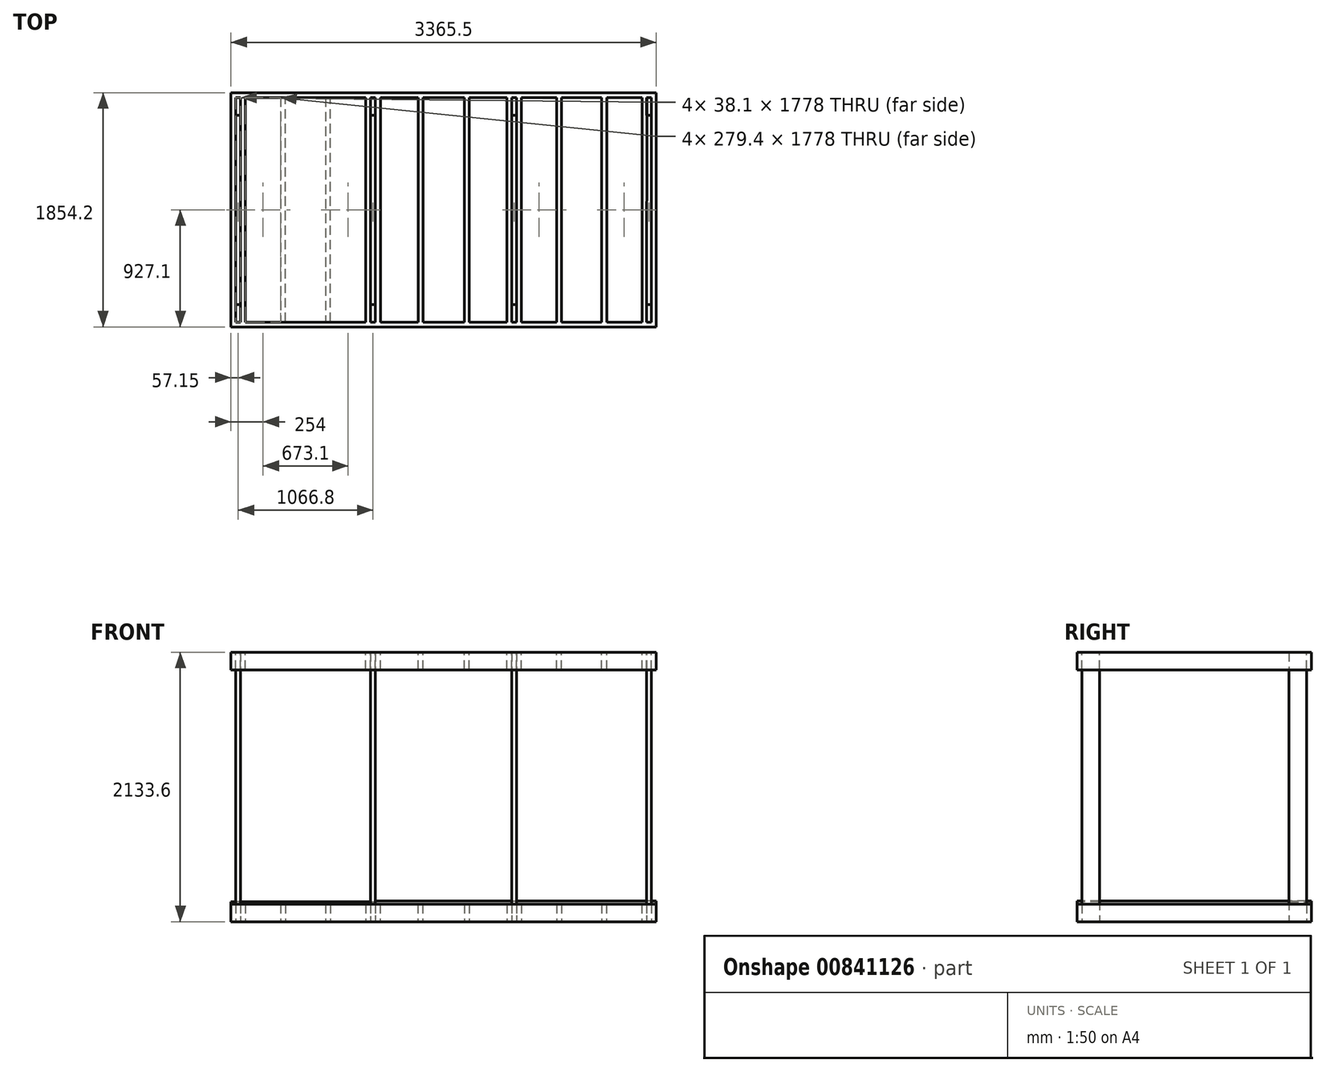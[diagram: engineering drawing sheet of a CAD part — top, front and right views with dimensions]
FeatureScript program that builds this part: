
annotation { "Feature Type Name" : "Feature", "Feature Type Description" : "" }
export const myFeature = defineFeature(function(context is Context, id is Id, definition is map)
    precondition{}
    {
        {
            var Q0;
            Q0=qCreatedBy(makeId("Top.planeOp"),FACE);
            var sketch = newSketch(context, id + "F0", { "sketchPlane" : qUnion([Q0])});
            skLineSegment(sketch, "E0.bottom", {"start": v(0, 0) * mm, "end": v(3365.5, 0) * mm});
            skLineSegment(sketch, "E0.top", {"start": v(0, -38.1) * mm, "end": v(1181.1, -38.1) * mm});
            skLineSegment(sketch, "E0.left", {"start": v(0, 0) * mm, "end": v(0, -38.1) * mm});
            skLineSegment(sketch, "E0.right", {"start": v(3365.5, 0) * mm, "end": v(3365.5, -38.1) * mm});
            skLineSegment(sketch, "E1.bottom", {"start": v(0, -38.1) * mm, "end": v(38.1, -38.1) * mm});
            skLineSegment(sketch, "E1.top", {"start": v(0, -1816.1) * mm, "end": v(38.1, -1816.1) * mm});
            skLineSegment(sketch, "E1.left", {"start": v(0, -38.1) * mm, "end": v(0, -1816.1) * mm});
            skLineSegment(sketch, "E1.right", {"start": v(38.1, -38.1) * mm, "end": v(38.1, -1816.1) * mm});
            skLineSegment(sketch, "E2.bottom", {"start": v(3251.2, -38.1) * mm, "end": v(3289.3, -38.1) * mm});
            skLineSegment(sketch, "E2.top", {"start": v(3251.2, -1816.1) * mm, "end": v(3289.3, -1816.1) * mm});
            skLineSegment(sketch, "E2.left", {"start": v(3251.2, -38.1) * mm, "end": v(3251.2, -1816.1) * mm});
            skLineSegment(sketch, "E2.right", {"start": v(3289.3, -38.1) * mm, "end": v(3289.3, -1816.1) * mm});
            skLineSegment(sketch, "E3.bottom", {"start": v(3365.5, -38.1) * mm, "end": v(3327.4, -38.1) * mm});
            skLineSegment(sketch, "E3.top", {"start": v(3365.5, -1816.1) * mm, "end": v(3327.4, -1816.1) * mm});
            skLineSegment(sketch, "E3.left", {"start": v(3365.5, -38.1) * mm, "end": v(3365.5, -1816.1) * mm});
            skLineSegment(sketch, "E3.right", {"start": v(3327.4, -38.1) * mm, "end": v(3327.4, -1816.1) * mm});
            skLineSegment(sketch, "E4.bottom", {"start": v(114.3, -38.1) * mm, "end": v(76.2, -38.1) * mm});
            skLineSegment(sketch, "E4.left", {"start": v(114.3, -38.1) * mm, "end": v(114.3, -1816.1) * mm});
            skLineSegment(sketch, "E4.right", {"start": v(76.2, -38.1) * mm, "end": v(76.2, -1816.1) * mm});
            skLineSegment(sketch, "E5.bottom", {"start": v(3365.5, -1854.2) * mm, "end": v(0, -1854.2) * mm});
            skLineSegment(sketch, "E5.top", {"start": v(3365.5, -1816.1) * mm, "end": v(0, -1816.1) * mm});
            skLineSegment(sketch, "E5.left", {"start": v(3365.5, -1816.1) * mm, "end": v(3365.5, -1854.2) * mm});
            skLineSegment(sketch, "E5.right", {"start": v(0, -1816.1) * mm, "end": v(0, -1854.2) * mm});
            skLineSegment(sketch, "E6.bottom", {"start": v(1066.8, -38.1) * mm, "end": v(1104.9, -38.1) * mm});
            skLineSegment(sketch, "E6.top", {"start": v(1066.8, -1816.1) * mm, "end": v(1104.9, -1816.1) * mm});
            skLineSegment(sketch, "E6.left", {"start": v(1066.8, -38.1) * mm, "end": v(1066.8, -1816.1) * mm});
            skLineSegment(sketch, "E6.right", {"start": v(1104.9, -38.1) * mm, "end": v(1104.9, -1816.1) * mm});
            skLineSegment(sketch, "E7.bottom", {"start": v(1143, -1816.1) * mm, "end": v(1181.1, -1816.1) * mm});
            skLineSegment(sketch, "E7.top", {"start": v(1143, -38.1) * mm, "end": v(1181.1, -38.1) * mm});
            skLineSegment(sketch, "E7.left", {"start": v(1143, -1816.1) * mm, "end": v(1143, -38.1) * mm});
            skLineSegment(sketch, "E7.right", {"start": v(1181.1, -1816.1) * mm, "end": v(1181.1, -38.1) * mm});
            skLineSegment(sketch, "E8.bottom", {"start": v(2184.4, -38.1) * mm, "end": v(2222.5, -38.1) * mm});
            skLineSegment(sketch, "E8.top", {"start": v(2184.4, -1816.1) * mm, "end": v(2222.5, -1816.1) * mm});
            skLineSegment(sketch, "E8.left", {"start": v(2184.4, -38.1) * mm, "end": v(2184.4, -1816.1) * mm});
            skLineSegment(sketch, "E8.right", {"start": v(2222.5, -38.1) * mm, "end": v(2222.5, -1816.1) * mm});
            skLineSegment(sketch, "E9.bottom", {"start": v(2260.6, -38.1) * mm, "end": v(2298.7, -38.1) * mm});
            skLineSegment(sketch, "E9.top", {"start": v(2260.6, -1816.1) * mm, "end": v(2298.7, -1816.1) * mm});
            skLineSegment(sketch, "E9.left", {"start": v(2260.6, -38.1) * mm, "end": v(2260.6, -1816.1) * mm});
            skLineSegment(sketch, "E9.right", {"start": v(2298.7, -38.1) * mm, "end": v(2298.7, -1816.1) * mm});
            skLineSegment(sketch, "E10", {"start": v(1123.95, -38.1) * mm, "end": v(1123.95, -1816.1) * mm, "construction": true});
            skLineSegment(sketch, "E11", {"start": v(2241.55, -38.1) * mm, "end": v(2241.55, -1816.1) * mm, "construction": true});
            skLineSegment(sketch, "E12", {"start": v(1181.1, -38.1) * mm, "end": v(3365.5, -38.1) * mm});
            skLineSegment(sketch, "E13", {"start": v(57.15, -38.1) * mm, "end": v(57.15, -1816.1) * mm, "construction": true});
            skLineSegment(sketch, "E14", {"start": v(3308.35, -38.1) * mm, "end": v(3308.35, -1816.1) * mm, "construction": true});
            skLineSegment(sketch, "E15", {"start": v(412.75, -38.1) * mm, "end": v(412.75, -1816.1) * mm, "construction": true});
            skLineSegment(sketch, "E16", {"start": v(768.35, -38.1) * mm, "end": v(768.35, -1816.1) * mm, "construction": true});
            skLineSegment(sketch, "E17", {"start": v(1498.6, -38.1) * mm, "end": v(1498.6, -1816.1) * mm, "construction": true});
            skLineSegment(sketch, "E18", {"start": v(1866.9, -38.1) * mm, "end": v(1866.9, -1816.1) * mm, "construction": true});
            skLineSegment(sketch, "E19", {"start": v(2597.15, -38.1) * mm, "end": v(2597.15, -1816.1) * mm, "construction": true});
            skLineSegment(sketch, "E20", {"start": v(2952.75, -38.1) * mm, "end": v(2952.75, -1816.1) * mm, "construction": true});
            skLineSegment(sketch, "E21", {"start": v(412.75, -927.1) * mm, "end": v(57.15, -927.1) * mm, "construction": true});
            skLineSegment(sketch, "E22", {"start": v(412.75, -927.1) * mm, "end": v(768.35, -927.1) * mm, "construction": true});
            skLineSegment(sketch, "E23", {"start": v(768.35, -927.1) * mm, "end": v(1123.95, -927.1) * mm, "construction": true});
            skLineSegment(sketch, "E24", {"start": v(1123.95, -927.1) * mm, "end": v(1498.6, -927.1) * mm, "construction": true});
            skLineSegment(sketch, "E25", {"start": v(1498.6, -927.1) * mm, "end": v(1866.9, -927.1) * mm, "construction": true});
            skLineSegment(sketch, "E26", {"start": v(1866.9, -927.1) * mm, "end": v(2241.55, -927.1) * mm, "construction": true});
            skLineSegment(sketch, "E27", {"start": v(2241.55, -927.1) * mm, "end": v(2597.15, -927.1) * mm, "construction": true});
            skLineSegment(sketch, "E28", {"start": v(2597.15, -927.1) * mm, "end": v(2952.75, -927.1) * mm, "construction": true});
            skLineSegment(sketch, "E29", {"start": v(2952.75, -927.1) * mm, "end": v(3308.35, -927.1) * mm, "construction": true});
            skLineSegment(sketch, "E30", {"start": v(393.7, -38.1) * mm, "end": v(393.7, -1816.1) * mm});
            skLineSegment(sketch, "E31", {"start": v(431.8, -1816.1) * mm, "end": v(431.8, -38.1) * mm});
            skLineSegment(sketch, "E32", {"start": v(749.3, -38.1) * mm, "end": v(749.3, -1816.1) * mm});
            skLineSegment(sketch, "E33", {"start": v(787.4, -1816.1) * mm, "end": v(787.4, -38.1) * mm});
            skLineSegment(sketch, "E34", {"start": v(1479.55, -38.1) * mm, "end": v(1479.55, -1816.1) * mm});
            skLineSegment(sketch, "E35", {"start": v(1517.65, -1816.1) * mm, "end": v(1517.65, -38.1) * mm});
            skLineSegment(sketch, "E36", {"start": v(1847.85, -38.1) * mm, "end": v(1847.85, -1816.1) * mm});
            skLineSegment(sketch, "E37", {"start": v(1885.95, -1816.1) * mm, "end": v(1885.95, -38.1) * mm});
            skLineSegment(sketch, "E38", {"start": v(2578.1, -38.1) * mm, "end": v(2578.1, -1816.1) * mm});
            skLineSegment(sketch, "E39", {"start": v(2616.2, -1816.1) * mm, "end": v(2616.2, -38.1) * mm});
            skLineSegment(sketch, "E40", {"start": v(2933.7, -38.1) * mm, "end": v(2933.7, -1816.1) * mm});
            skLineSegment(sketch, "E41", {"start": v(2971.8, -1816.1) * mm, "end": v(2971.8, -38.1) * mm});
            skLineSegment(sketch, "E42", {"start": v(393.7, -447.33) * mm, "end": v(412.75, -447.33) * mm, "construction": true});
            skLineSegment(sketch, "E43", {"start": v(412.75, -447.33) * mm, "end": v(431.8, -447.33) * mm, "construction": true});
            skLineSegment(sketch, "E44", {"start": v(768.35, -464.24) * mm, "end": v(787.4, -464.24) * mm, "construction": true});
            skLineSegment(sketch, "E45", {"start": v(1479.55, -447.33) * mm, "end": v(1498.6, -447.33) * mm, "construction": true});
            skLineSegment(sketch, "E46", {"start": v(1498.6, -447.33) * mm, "end": v(1517.65, -447.33) * mm, "construction": true});
            skLineSegment(sketch, "E47", {"start": v(1866.9, -447.33) * mm, "end": v(1885.95, -447.33) * mm, "construction": true});
            skLineSegment(sketch, "E48", {"start": v(1847.85, -447.33) * mm, "end": v(1866.9, -447.33) * mm, "construction": true});
            skLineSegment(sketch, "E49", {"start": v(2578.1, -447.33) * mm, "end": v(2597.15, -447.33) * mm, "construction": true});
            skLineSegment(sketch, "E50", {"start": v(2597.15, -447.33) * mm, "end": v(2616.2, -447.33) * mm, "construction": true});
            skLineSegment(sketch, "E51", {"start": v(2933.7, -447.33) * mm, "end": v(2952.75, -447.33) * mm, "construction": true});
            skLineSegment(sketch, "E52", {"start": v(2952.75, -447.33) * mm, "end": v(2971.8, -447.33) * mm, "construction": true});
            skLineSegment(sketch, "E53", {"start": v(768.35, -464.24) * mm, "end": v(749.3, -464.24) * mm, "construction": true});
            skSolve(sketch);
        }
        {
            var Q0;
            Q0=makeQuery(id+"F0.imprint","IMPRINT",FACE,{"disambiguationData":[TD([[makeQuery(id+"F0.imprint","IMPRINT",EDGE,{"derivedFrom":sQuery(id+"F0.wireOp",EDGE,"E0.bottom")}),-1.0]])]});
            var Q1;
            Q1=makeQuery(id+"F0.imprint","IMPRINT",FACE,{"disambiguationData":[TD([[makeQuery(id+"F0.imprint","IMPRINT",EDGE,{"derivedFrom":sQuery(id+"F0.wireOp",EDGE,"E3.bottom")}),1.0]])]});
            var Q2;
            Q2=makeQuery(id+"F0.imprint","IMPRINT",FACE,{"disambiguationData":[TD([[makeQuery(id+"F0.imprint","IMPRINT",EDGE,{"derivedFrom":sQuery(id+"F0.wireOp",EDGE,"E2.bottom")}),-1.0]])]});
            var Q3;
            {var subQ18=sQuery(id+"F0.wireOp",EDGE,"E1.top");Q3=makeQuery(id+"F0.imprint","IMPRINT",FACE,{"disambiguationData":[TD([[makeQuery(id+"F0.imprint","IMPRINT",EDGE,{"derivedFrom":subQ18}),-1.0]])]});}
            var Q4;
            Q4=makeQuery(id+"F0.imprint","IMPRINT",FACE,{"disambiguationData":[TD([[makeQuery(id+"F0.imprint","IMPRINT",EDGE,{"derivedFrom":sQuery(id+"F0.wireOp",EDGE,"E1.top")}),1.0]])]});
            var Q5;
            {var subQ2=sQuery(id+"F0.wireOp",EDGE,"E4.left");Q5=makeQuery(id+"F0.imprint","IMPRINT",FACE,{"disambiguationData":[TD([[makeQuery(id+"F0.imprint","IMPRINT",EDGE,{"derivedFrom":subQ2}),-1.0]])]});}
            var Q6;
            {var subQ0=sQuery(id+"F0.wireOp",EDGE,"E6.left");Q6=makeQuery(id+"F0.imprint","IMPRINT",FACE,{"disambiguationData":[TD([[makeQuery(id+"F0.imprint","IMPRINT",EDGE,{"derivedFrom":subQ0}),1.0]])]});}
            var Q7;
            {var subQ0=sQuery(id+"F0.wireOp",EDGE,"E7.left");Q7=makeQuery(id+"F0.imprint","IMPRINT",FACE,{"disambiguationData":[TD([[makeQuery(id+"F0.imprint","IMPRINT",EDGE,{"derivedFrom":subQ0}),-1.0]])]});}
            var Q8;
            Q8=makeQuery(id+"F0.imprint","IMPRINT",FACE,{"disambiguationData":[TD([[makeQuery(id+"F0.imprint","IMPRINT",EDGE,{"derivedFrom":sQuery(id+"F0.wireOp",EDGE,"E8.bottom")}),-1.0]])]});
            var Q9;
            Q9=makeQuery(id+"F0.imprint","IMPRINT",FACE,{"disambiguationData":[TD([[makeQuery(id+"F0.imprint","IMPRINT",EDGE,{"derivedFrom":sQuery(id+"F0.wireOp",EDGE,"E9.bottom")}),-1.0]])]});
            var Q10;
            Q10=makeQuery(id+"F0.imprint","IMPRINT",FACE,{"disambiguationData":[TD([[makeQuery(id+"F0.imprint","IMPRINT",EDGE,{"derivedFrom":sQuery(id+"F0.wireOp",EDGE,"E2.bottom")}),-1.0]])]});
            var Q11;
            Q11=makeQuery(id+"F0.imprint","IMPRINT",FACE,{"disambiguationData":[TD([[makeQuery(id+"F0.imprint","IMPRINT",EDGE,{"derivedFrom":sQuery(id+"F0.wireOp",EDGE,"E3.bottom")}),1.0]])]});
            var Q12;
            {var subQ2=sQuery(id+"F0.wireOp",EDGE,"E30");Q12=makeQuery(id+"F0.imprint","IMPRINT",FACE,{"disambiguationData":[TD([[makeQuery(id+"F0.imprint","IMPRINT",EDGE,{"derivedFrom":subQ2}),1.0]])]});}
            var Q13;
            {var subQ0=sQuery(id+"F0.wireOp",EDGE,"E32");Q13=makeQuery(id+"F0.imprint","IMPRINT",FACE,{"disambiguationData":[TD([[makeQuery(id+"F0.imprint","IMPRINT",EDGE,{"derivedFrom":subQ0}),1.0]])]});}
            var Q14;
            {var subQ0=sQuery(id+"F0.wireOp",EDGE,"E34");Q14=makeQuery(id+"F0.imprint","IMPRINT",FACE,{"disambiguationData":[TD([[makeQuery(id+"F0.imprint","IMPRINT",EDGE,{"derivedFrom":subQ0}),1.0]])]});}
            var Q15;
            {var subQ0=sQuery(id+"F0.wireOp",EDGE,"E36");Q15=makeQuery(id+"F0.imprint","IMPRINT",FACE,{"disambiguationData":[TD([[makeQuery(id+"F0.imprint","IMPRINT",EDGE,{"derivedFrom":subQ0}),1.0]])]});}
            var Q16;
            {var subQ0=sQuery(id+"F0.wireOp",EDGE,"E38");Q16=makeQuery(id+"F0.imprint","IMPRINT",FACE,{"disambiguationData":[TD([[makeQuery(id+"F0.imprint","IMPRINT",EDGE,{"derivedFrom":subQ0}),1.0]])]});}
            var Q17;
            {var subQ0=sQuery(id+"F0.wireOp",EDGE,"E40");Q17=makeQuery(id+"F0.imprint","IMPRINT",FACE,{"disambiguationData":[TD([[makeQuery(id+"F0.imprint","IMPRINT",EDGE,{"derivedFrom":subQ0}),1.0]])]});}
            extrude(context, id + "F1", {"entities" : qUnion([Q0, Q1, Q2, Q3, Q4, Q5, Q6, Q7, Q8, Q9, Q10, Q11, Q12, Q13, Q14, Q15, Q16, Q17]), "depth" : 139.7 * mm, "offsetDistance" : 25.4 * mm});
        }
        {
            var Q0;
            Q0=makeQuery(id+"F1.opExtrude","CAP_FACE",FACE,{"disambiguationData":[OSD([sQuery(id+"F0.wireOp",EDGE,"E0.bottom"),sQuery(id+"F0.wireOp",EDGE,"E0.top"),sQuery(id+"F0.wireOp",EDGE,"E0.left"),sQuery(id+"F0.wireOp",EDGE,"E0.right"),sQuery(id+"F0.wireOp",EDGE,"E1.left"),sQuery(id+"F0.wireOp",EDGE,"E1.right"),sQuery(id+"F0.wireOp",EDGE,"E2.left"),sQuery(id+"F0.wireOp",EDGE,"E2.right"),sQuery(id+"F0.wireOp",EDGE,"E3.left"),sQuery(id+"F0.wireOp",EDGE,"E3.right"),sQuery(id+"F0.wireOp",EDGE,"E4.left"),sQuery(id+"F0.wireOp",EDGE,"E4.right"),sQuery(id+"F0.wireOp",EDGE,"E5.bottom"),sQuery(id+"F0.wireOp",EDGE,"E5.top"),sQuery(id+"F0.wireOp",EDGE,"E5.left"),sQuery(id+"F0.wireOp",EDGE,"E5.right"),sQuery(id+"F0.wireOp",EDGE,"E6.left"),sQuery(id+"F0.wireOp",EDGE,"E6.right"),sQuery(id+"F0.wireOp",EDGE,"E7.left"),sQuery(id+"F0.wireOp",EDGE,"E7.right"),sQuery(id+"F0.wireOp",EDGE,"E8.left"),sQuery(id+"F0.wireOp",EDGE,"E8.right"),sQuery(id+"F0.wireOp",EDGE,"E9.left"),sQuery(id+"F0.wireOp",EDGE,"E9.right"),sQuery(id+"F0.wireOp",EDGE,"E12"),sQuery(id+"F0.wireOp",EDGE,"E30"),sQuery(id+"F0.wireOp",EDGE,"E31"),sQuery(id+"F0.wireOp",EDGE,"E32"),sQuery(id+"F0.wireOp",EDGE,"E33"),sQuery(id+"F0.wireOp",EDGE,"E34"),sQuery(id+"F0.wireOp",EDGE,"E35"),sQuery(id+"F0.wireOp",EDGE,"E36"),sQuery(id+"F0.wireOp",EDGE,"E37"),sQuery(id+"F0.wireOp",EDGE,"E38"),sQuery(id+"F0.wireOp",EDGE,"E39"),sQuery(id+"F0.wireOp",EDGE,"E40"),sQuery(id+"F0.wireOp",EDGE,"E41")])],"isStart":true});
            var sketch = newSketch(context, id + "F2", { "sketchPlane" : qUnion([Q0])});
            skLineSegment(sketch, "E54.bottom", {"start": v(38.1, 1816.1) * mm, "end": v(76.2, 1816.1) * mm});
            skLineSegment(sketch, "E54.top", {"start": v(38.1, 1676.4) * mm, "end": v(76.2, 1676.4) * mm});
            skLineSegment(sketch, "E54.left", {"start": v(38.1, 1816.1) * mm, "end": v(38.1, 1676.4) * mm});
            skLineSegment(sketch, "E54.right", {"start": v(76.2, 1816.1) * mm, "end": v(76.2, 1676.4) * mm});
            skLineSegment(sketch, "E55.bottom", {"start": v(1104.9, 1816.1) * mm, "end": v(1143, 1816.1) * mm});
            skLineSegment(sketch, "E55.top", {"start": v(1104.9, 1676.4) * mm, "end": v(1143, 1676.4) * mm});
            skLineSegment(sketch, "E55.left", {"start": v(1104.9, 1816.1) * mm, "end": v(1104.9, 1676.4) * mm});
            skLineSegment(sketch, "E55.right", {"start": v(1143, 1816.1) * mm, "end": v(1143, 1676.4) * mm});
            skLineSegment(sketch, "E56.bottom", {"start": v(2222.5, 1816.1) * mm, "end": v(2260.6, 1816.1) * mm});
            skLineSegment(sketch, "E56.top", {"start": v(2222.5, 1676.4) * mm, "end": v(2260.6, 1676.4) * mm});
            skLineSegment(sketch, "E56.left", {"start": v(2222.5, 1816.1) * mm, "end": v(2222.5, 1676.4) * mm});
            skLineSegment(sketch, "E56.right", {"start": v(2260.6, 1816.1) * mm, "end": v(2260.6, 1676.4) * mm});
            skLineSegment(sketch, "E57.bottom", {"start": v(3289.3, 1816.1) * mm, "end": v(3327.4, 1816.1) * mm});
            skLineSegment(sketch, "E57.top", {"start": v(3289.3, 1676.4) * mm, "end": v(3327.4, 1676.4) * mm});
            skLineSegment(sketch, "E57.left", {"start": v(3289.3, 1816.1) * mm, "end": v(3289.3, 1676.4) * mm});
            skLineSegment(sketch, "E57.right", {"start": v(3327.4, 1816.1) * mm, "end": v(3327.4, 1676.4) * mm});
            skLineSegment(sketch, "E58.bottom", {"start": v(3289.3, 38.1) * mm, "end": v(3327.4, 38.1) * mm});
            skLineSegment(sketch, "E58.top", {"start": v(3289.3, 177.8) * mm, "end": v(3327.4, 177.8) * mm});
            skLineSegment(sketch, "E58.left", {"start": v(3289.3, 38.1) * mm, "end": v(3289.3, 177.8) * mm});
            skLineSegment(sketch, "E58.right", {"start": v(3327.4, 38.1) * mm, "end": v(3327.4, 177.8) * mm});
            skLineSegment(sketch, "E59.bottom", {"start": v(2222.5, 38.1) * mm, "end": v(2260.6, 38.1) * mm});
            skLineSegment(sketch, "E59.top", {"start": v(2222.5, 177.8) * mm, "end": v(2260.6, 177.8) * mm});
            skLineSegment(sketch, "E59.left", {"start": v(2222.5, 38.1) * mm, "end": v(2222.5, 177.8) * mm});
            skLineSegment(sketch, "E59.right", {"start": v(2260.6, 38.1) * mm, "end": v(2260.6, 177.8) * mm});
            skLineSegment(sketch, "E60.bottom", {"start": v(1104.9, 38.1) * mm, "end": v(1143, 38.1) * mm});
            skLineSegment(sketch, "E60.top", {"start": v(1104.9, 177.8) * mm, "end": v(1143, 177.8) * mm});
            skLineSegment(sketch, "E60.left", {"start": v(1104.9, 38.1) * mm, "end": v(1104.9, 177.8) * mm});
            skLineSegment(sketch, "E60.right", {"start": v(1143, 38.1) * mm, "end": v(1143, 177.8) * mm});
            skLineSegment(sketch, "E61.bottom", {"start": v(38.1, 38.1) * mm, "end": v(76.2, 38.1) * mm});
            skLineSegment(sketch, "E61.top", {"start": v(38.1, 177.8) * mm, "end": v(76.2, 177.8) * mm});
            skLineSegment(sketch, "E61.left", {"start": v(38.1, 38.1) * mm, "end": v(38.1, 177.8) * mm});
            skLineSegment(sketch, "E61.right", {"start": v(76.2, 38.1) * mm, "end": v(76.2, 177.8) * mm});
            skSolve(sketch);
        }
        {
            var Q0;
            Q0=makeQuery(id+"F2.imprint","IMPRINT",FACE,{"disambiguationData":[TD([[makeQuery(id+"F2.imprint","IMPRINT",EDGE,{"derivedFrom":sQuery(id+"F2.wireOp",EDGE,"E61.bottom")}),1.0]])]});
            var Q1;
            Q1=makeQuery(id+"F2.imprint","IMPRINT",FACE,{"disambiguationData":[TD([[makeQuery(id+"F2.imprint","IMPRINT",EDGE,{"derivedFrom":sQuery(id+"F2.wireOp",EDGE,"E60.bottom")}),1.0]])]});
            var Q2;
            Q2=makeQuery(id+"F2.imprint","IMPRINT",FACE,{"disambiguationData":[TD([[makeQuery(id+"F2.imprint","IMPRINT",EDGE,{"derivedFrom":sQuery(id+"F2.wireOp",EDGE,"E59.bottom")}),1.0]])]});
            var Q3;
            Q3=makeQuery(id+"F2.imprint","IMPRINT",FACE,{"disambiguationData":[TD([[makeQuery(id+"F2.imprint","IMPRINT",EDGE,{"derivedFrom":sQuery(id+"F2.wireOp",EDGE,"E58.bottom")}),1.0]])]});
            var Q4;
            Q4=makeQuery(id+"F2.imprint","IMPRINT",FACE,{"disambiguationData":[TD([[makeQuery(id+"F2.imprint","IMPRINT",EDGE,{"derivedFrom":sQuery(id+"F2.wireOp",EDGE,"E54.bottom")}),1.0]])]});
            var Q5;
            Q5=makeQuery(id+"F2.imprint","IMPRINT",FACE,{"disambiguationData":[TD([[makeQuery(id+"F2.imprint","IMPRINT",EDGE,{"derivedFrom":sQuery(id+"F2.wireOp",EDGE,"E55.bottom")}),1.0]])]});
            var Q6;
            Q6=makeQuery(id+"F2.imprint","IMPRINT",FACE,{"disambiguationData":[TD([[makeQuery(id+"F2.imprint","IMPRINT",EDGE,{"derivedFrom":sQuery(id+"F2.wireOp",EDGE,"E56.bottom")}),1.0]])]});
            var Q7;
            Q7=makeQuery(id+"F2.imprint","IMPRINT",FACE,{"disambiguationData":[TD([[makeQuery(id+"F2.imprint","IMPRINT",EDGE,{"derivedFrom":sQuery(id+"F2.wireOp",EDGE,"E57.bottom")}),1.0]])]});
            extrude(context, id + "F3", {"entities" : qUnion([Q0, Q1, Q2, Q3, Q4, Q5, Q6, Q7]), "oppositeDirection" : true, "depth" : 2133.6 * mm, "offsetDistance" : 25.4 * mm});
        }
        {
            var Q0;
            Q0=makeQuery(id+"F3.opExtrude","CAP_FACE",FACE,{"disambiguationData":[OSD([sQuery(id+"F2.wireOp",EDGE,"E57.bottom"),sQuery(id+"F2.wireOp",EDGE,"E57.top"),sQuery(id+"F2.wireOp",EDGE,"E57.left"),sQuery(id+"F2.wireOp",EDGE,"E57.right")])],"isStart":false});
            var sketch = newSketch(context, id + "F4", { "sketchPlane" : qUnion([Q0])});
            skLineSegment(sketch, "E62", {"start": v(3327.4, -1816.1) * mm, "end": v(38.1, -1816.1) * mm});
            skLineSegment(sketch, "E63", {"start": v(38.1, -1816.1) * mm, "end": v(38.1, -38.1) * mm});
            skLineSegment(sketch, "E64", {"start": v(38.1, -38.1) * mm, "end": v(3327.4, -38.1) * mm});
            skLineSegment(sketch, "E65", {"start": v(3327.4, -38.1) * mm, "end": v(3327.4, -1816.1) * mm});
            skLineSegment(sketch, "E66", {"start": v(3365.5, -1854.2) * mm, "end": v(3365.5, 0) * mm});
            skLineSegment(sketch, "E67", {"start": v(3365.5, 0) * mm, "end": v(0, 0) * mm});
            skLineSegment(sketch, "E68", {"start": v(0, 0) * mm, "end": v(0, -1854.2) * mm});
            skLineSegment(sketch, "E69", {"start": v(0, -1854.2) * mm, "end": v(3365.5, -1854.2) * mm});
            skLineSegment(sketch, "E70", {"start": v(3290.38, -38.1) * mm, "end": v(3289.3, -1816.1) * mm});
            skLineSegment(sketch, "E71", {"start": v(3252.14, -1816.1) * mm, "end": v(3252.14, -38.1) * mm});
            skLineSegment(sketch, "E72", {"start": v(2972.63, -38.1) * mm, "end": v(2972.63, -1816.1) * mm});
            skLineSegment(sketch, "E73", {"start": v(2933.24, -1816.1) * mm, "end": v(2933.24, -38.1) * mm});
            skLineSegment(sketch, "E74", {"start": v(2616.6, -38.1) * mm, "end": v(2616.6, -1816.1) * mm});
            skLineSegment(sketch, "E75", {"start": v(2577.63, -1816.1) * mm, "end": v(2577.63, -38.1) * mm});
            skLineSegment(sketch, "E76", {"start": v(2299.35, -38.1) * mm, "end": v(2299.35, -1816.1) * mm});
            skLineSegment(sketch, "E77", {"start": v(2260.87, -1816.1) * mm, "end": v(2260.87, -38.1) * mm});
            skLineSegment(sketch, "E78", {"start": v(2222.09, -38.1) * mm, "end": v(2222.09, -1816.1) * mm});
            skLineSegment(sketch, "E79", {"start": v(2184.41, -1816.1) * mm, "end": v(2184.41, -38.1) * mm});
            skLineSegment(sketch, "E80", {"start": v(1886.34, -38.1) * mm, "end": v(1886.34, -1816.1) * mm});
            skLineSegment(sketch, "E81", {"start": v(1848.29, -1816.1) * mm, "end": v(1848.29, -38.1) * mm});
            skLineSegment(sketch, "E82", {"start": v(1518.71, -38.1) * mm, "end": v(1518.71, -1816.1) * mm});
            skLineSegment(sketch, "E83", {"start": v(1480.52, -1816.1) * mm, "end": v(1480.52, -38.1) * mm});
            skLineSegment(sketch, "E84", {"start": v(1183.17, -38.1) * mm, "end": v(1183.17, -1816.1) * mm});
            skLineSegment(sketch, "E85", {"start": v(1143.26, -1816.1) * mm, "end": v(1143.26, -38.1) * mm});
            skLineSegment(sketch, "E86", {"start": v(1105.01, -1816.1) * mm, "end": v(1105.01, -38.1) * mm});
            skLineSegment(sketch, "E87", {"start": v(1065.91, -38.1) * mm, "end": v(1065.91, -1816.1) * mm});
            skLineSegment(sketch, "E88", {"start": v(76.3, -1816.1) * mm, "end": v(76.3, -38.1) * mm});
            skLineSegment(sketch, "E89", {"start": v(114.7, -38.1) * mm, "end": v(114.7, -1816.1) * mm});
            skSolve(sketch);
        }
        {
            var Q0;
            Q0 = qSketchRegion(id + "F4", true);
            var Q1;
            {var subQ5=sQuery(id+"F4.wireOp",EDGE,"E71");Q1=makeQuery(id+"F4.imprint","IMPRINT",FACE,{"disambiguationData":[TD([[makeQuery(id+"F4.imprint","IMPRINT",EDGE,{"derivedFrom":subQ5}),-1.0]])]});}
            var Q2;
            {var subQ0=sQuery(id+"F4.wireOp",EDGE,"E72");Q2=makeQuery(id+"F4.imprint","IMPRINT",FACE,{"disambiguationData":[TD([[makeQuery(id+"F4.imprint","IMPRINT",EDGE,{"derivedFrom":subQ0}),-1.0]])]});}
            var Q3;
            {var subQ0=sQuery(id+"F4.wireOp",EDGE,"E74");Q3=makeQuery(id+"F4.imprint","IMPRINT",FACE,{"disambiguationData":[TD([[makeQuery(id+"F4.imprint","IMPRINT",EDGE,{"derivedFrom":subQ0}),-1.0]])]});}
            var Q4;
            {var subQ0=sQuery(id+"F4.wireOp",EDGE,"E76");Q4=makeQuery(id+"F4.imprint","IMPRINT",FACE,{"disambiguationData":[TD([[makeQuery(id+"F4.imprint","IMPRINT",EDGE,{"derivedFrom":subQ0}),-1.0]])]});}
            var Q5;
            {var subQ0=sQuery(id+"F4.wireOp",EDGE,"E78");Q5=makeQuery(id+"F4.imprint","IMPRINT",FACE,{"disambiguationData":[TD([[makeQuery(id+"F4.imprint","IMPRINT",EDGE,{"derivedFrom":subQ0}),-1.0]])]});}
            var Q6;
            {var subQ0=sQuery(id+"F4.wireOp",EDGE,"E80");Q6=makeQuery(id+"F4.imprint","IMPRINT",FACE,{"disambiguationData":[TD([[makeQuery(id+"F4.imprint","IMPRINT",EDGE,{"derivedFrom":subQ0}),-1.0]])]});}
            var Q7;
            {var subQ0=sQuery(id+"F4.wireOp",EDGE,"E82");Q7=makeQuery(id+"F4.imprint","IMPRINT",FACE,{"disambiguationData":[TD([[makeQuery(id+"F4.imprint","IMPRINT",EDGE,{"derivedFrom":subQ0}),-1.0]])]});}
            var Q8;
            {var subQ0=sQuery(id+"F4.wireOp",EDGE,"E84");Q8=makeQuery(id+"F4.imprint","IMPRINT",FACE,{"disambiguationData":[TD([[makeQuery(id+"F4.imprint","IMPRINT",EDGE,{"derivedFrom":subQ0}),-1.0]])]});}
            var Q9;
            {var subQ0=sQuery(id+"F4.wireOp",EDGE,"E86");Q9=makeQuery(id+"F4.imprint","IMPRINT",FACE,{"disambiguationData":[TD([[makeQuery(id+"F4.imprint","IMPRINT",EDGE,{"derivedFrom":subQ0}),1.0]])]});}
            var Q10;
            {var subQ0=sQuery(id+"F4.wireOp",EDGE,"E88");Q10=makeQuery(id+"F4.imprint","IMPRINT",FACE,{"disambiguationData":[TD([[makeQuery(id+"F4.imprint","IMPRINT",EDGE,{"derivedFrom":subQ0}),-1.0]])]});}
            extrude(context, id + "F5", {"entities" : qUnion([Q0, Q1, Q2, Q3, Q4, Q5, Q6, Q7, Q8, Q9, Q10]), "oppositeDirection" : true, "depth" : 139.7 * mm, "offsetDistance" : 25.4 * mm});
        }
        {
            var Q0;
            Q0=makeQuery(id+"F1.opExtrude","CAP_FACE",FACE,{"disambiguationData":[OSD([sQuery(id+"F0.wireOp",EDGE,"E0.bottom"),sQuery(id+"F0.wireOp",EDGE,"E0.top"),sQuery(id+"F0.wireOp",EDGE,"E0.left"),sQuery(id+"F0.wireOp",EDGE,"E0.right"),sQuery(id+"F0.wireOp",EDGE,"E1.left"),sQuery(id+"F0.wireOp",EDGE,"E1.right"),sQuery(id+"F0.wireOp",EDGE,"E2.left"),sQuery(id+"F0.wireOp",EDGE,"E2.right"),sQuery(id+"F0.wireOp",EDGE,"E3.left"),sQuery(id+"F0.wireOp",EDGE,"E3.right"),sQuery(id+"F0.wireOp",EDGE,"E4.left"),sQuery(id+"F0.wireOp",EDGE,"E4.right"),sQuery(id+"F0.wireOp",EDGE,"E5.bottom"),sQuery(id+"F0.wireOp",EDGE,"E5.top"),sQuery(id+"F0.wireOp",EDGE,"E5.left"),sQuery(id+"F0.wireOp",EDGE,"E5.right"),sQuery(id+"F0.wireOp",EDGE,"E6.left"),sQuery(id+"F0.wireOp",EDGE,"E6.right"),sQuery(id+"F0.wireOp",EDGE,"E7.left"),sQuery(id+"F0.wireOp",EDGE,"E7.right"),sQuery(id+"F0.wireOp",EDGE,"E8.left"),sQuery(id+"F0.wireOp",EDGE,"E8.right"),sQuery(id+"F0.wireOp",EDGE,"E9.left"),sQuery(id+"F0.wireOp",EDGE,"E9.right"),sQuery(id+"F0.wireOp",EDGE,"E12"),sQuery(id+"F0.wireOp",EDGE,"E30"),sQuery(id+"F0.wireOp",EDGE,"E31"),sQuery(id+"F0.wireOp",EDGE,"E32"),sQuery(id+"F0.wireOp",EDGE,"E33"),sQuery(id+"F0.wireOp",EDGE,"E34"),sQuery(id+"F0.wireOp",EDGE,"E35"),sQuery(id+"F0.wireOp",EDGE,"E36"),sQuery(id+"F0.wireOp",EDGE,"E37"),sQuery(id+"F0.wireOp",EDGE,"E38"),sQuery(id+"F0.wireOp",EDGE,"E39"),sQuery(id+"F0.wireOp",EDGE,"E40"),sQuery(id+"F0.wireOp",EDGE,"E41")])],"isStart":false});
            var sketch = newSketch(context, id + "F6", { "sketchPlane" : qUnion([Q0])});
            skLineSegment(sketch, "E90", {"start": v(0, -177.8) * mm, "end": v(76.2, -177.8) * mm});
            skLineSegment(sketch, "E91", {"start": v(76.2, -177.8) * mm, "end": v(76.2, 0) * mm});
            skLineSegment(sketch, "E92", {"start": v(76.2, 0) * mm, "end": v(1104.9, 0) * mm});
            skLineSegment(sketch, "E93", {"start": v(1104.9, 0) * mm, "end": v(1104.9, -177.8) * mm});
            skLineSegment(sketch, "E94", {"start": v(1104.9, -1854.2) * mm, "end": v(76.2, -1854.2) * mm});
            skLineSegment(sketch, "E95", {"start": v(76.2, -1854.2) * mm, "end": v(76.2, -1676.4) * mm});
            skLineSegment(sketch, "E96", {"start": v(76.2, -1676.4) * mm, "end": v(0, -1676.4) * mm});
            skLineSegment(sketch, "E97", {"start": v(0, -1676.4) * mm, "end": v(0, -177.8) * mm});
            skLineSegment(sketch, "E98", {"start": v(1104.9, -1676.4) * mm, "end": v(1143, -1676.4) * mm});
            skLineSegment(sketch, "E99", {"start": v(1143, -1676.4) * mm, "end": v(1143, -177.8) * mm});
            skLineSegment(sketch, "E100", {"start": v(1143, -177.8) * mm, "end": v(1104.9, -177.8) * mm});
            skLineSegment(sketch, "E101.trimOffspring", {"start": v(1104.9, -1676.4) * mm, "end": v(1104.9, -1854.2) * mm});
            skLineSegment(sketch, "E102", {"start": v(2222.5, 0) * mm, "end": v(2222.5, -1854.2) * mm});
            skLineSegment(sketch, "E103", {"start": v(2222.5, -1854.2) * mm, "end": v(1143, -1854.2) * mm});
            skLineSegment(sketch, "E104", {"start": v(1143, -1854.2) * mm, "end": v(1143, 0) * mm});
            skLineSegment(sketch, "E105", {"start": v(1143, 0) * mm, "end": v(2222.5, 0) * mm});
            skLineSegment(sketch, "E106", {"start": v(2222.5, -177.8) * mm, "end": v(2260.6, -177.8) * mm});
            skLineSegment(sketch, "E107", {"start": v(2260.6, -177.8) * mm, "end": v(2260.6, 0) * mm});
            skLineSegment(sketch, "E108", {"start": v(2260.6, 0) * mm, "end": v(3289.3, 0) * mm});
            skLineSegment(sketch, "E109", {"start": v(3289.3, 0) * mm, "end": v(3289.3, -177.8) * mm});
            skLineSegment(sketch, "E110", {"start": v(3289.3, -177.8) * mm, "end": v(3365.5, -177.8) * mm});
            skLineSegment(sketch, "E111", {"start": v(3365.5, -177.8) * mm, "end": v(3365.5, -1676.4) * mm});
            skLineSegment(sketch, "E112", {"start": v(3365.5, -1676.4) * mm, "end": v(3289.3, -1676.4) * mm});
            skLineSegment(sketch, "E113", {"start": v(3289.3, -1676.4) * mm, "end": v(3289.3, -1854.2) * mm});
            skLineSegment(sketch, "E114", {"start": v(3289.3, -1854.2) * mm, "end": v(2260.6, -1854.2) * mm});
            skLineSegment(sketch, "E115", {"start": v(2260.6, -1854.2) * mm, "end": v(2260.6, -1676.4) * mm});
            skLineSegment(sketch, "E116", {"start": v(2260.6, -1676.4) * mm, "end": v(2222.5, -1676.4) * mm});
            skLineSegment(sketch, "E117", {"start": v(2222.5, -1676.4) * mm, "end": v(2222.5, -177.8) * mm});
            skSolve(sketch);
        }
        {
            var Q0;
            {var subQ13=sQuery(id+"F6.wireOp",EDGE,"E92");Q0=makeQuery(id+"F6.imprint","IMPRINT",FACE,{"disambiguationData":[TD([[makeQuery(id+"F6.imprint","IMPRINT",EDGE,{"derivedFrom":subQ13}),-1.0]])]});}
            var Q1;
            {var subQ0=sQuery(id+"F6.wireOp",EDGE,"E97");Q1=makeQuery(id+"F6.imprint","IMPRINT",FACE,{"disambiguationData":[TD([[makeQuery(id+"F6.imprint","IMPRINT",EDGE,{"derivedFrom":subQ0}),1.0]])]});}
            var Q2;
            {var subQ0=sQuery(id+"F6.wireOp",EDGE,"E90");var subQ3=makeQuery(id+"F1.opExtrude","CAP_EDGE",EDGE,{"disambiguationData":[OSD([sQuery(id+"F0.wireOp",EDGE,"E1.right")])],"isStart":false});var subQ4=makeQuery(id+"F6.imprint","INTERSECT",VERTEX,{"derivedFrom":[subQ3,subQ0]});Q2=makeQuery(id+"F6.imprint","IMPRINT",FACE,{"disambiguationData":[TD([[makeQuery(id+"F6.imprint","IMPRINT",EDGE,{"disambiguationData":[TD([[subQ4,-1.0]])],"derivedFrom":subQ3}),1.0]])]});}
            var Q3;
            {var subQ0=sQuery(id+"F6.wireOp",EDGE,"E98");Q3=makeQuery(id+"F6.imprint","IMPRINT",FACE,{"disambiguationData":[TD([[makeQuery(id+"F6.imprint","IMPRINT",EDGE,{"derivedFrom":subQ0}),1.0]])]});}
            var Q4;
            {var subQ0=sQuery(id+"F0.wireOp",EDGE,"E4.left");Q4=makeQuery(id+"F6.imprint","IMPRINT",FACE,{"disambiguationData":[TD([[makeQuery(id+"F6.imprint","IMPRINT",EDGE,{"derivedFrom":makeQuery(id+"F1.opExtrude","CAP_EDGE",EDGE,{"disambiguationData":[OSD([subQ0])],"isStart":false})}),1.0]])]});}
            var Q5;
            {var subQ0=sQuery(id+"F0.wireOp",EDGE,"E31");Q5=makeQuery(id+"F6.imprint","IMPRINT",FACE,{"disambiguationData":[TD([[makeQuery(id+"F6.imprint","IMPRINT",EDGE,{"derivedFrom":makeQuery(id+"F1.opExtrude","CAP_EDGE",EDGE,{"disambiguationData":[OSD([subQ0])],"isStart":false})}),-1.0]])]});}
            var Q6;
            {var subQ0=sQuery(id+"F0.wireOp",EDGE,"E6.left");Q6=makeQuery(id+"F6.imprint","IMPRINT",FACE,{"disambiguationData":[TD([[makeQuery(id+"F6.imprint","IMPRINT",EDGE,{"derivedFrom":makeQuery(id+"F1.opExtrude","CAP_EDGE",EDGE,{"disambiguationData":[OSD([subQ0])],"isStart":false})}),-1.0]])]});}
            extrude(context, id + "F7", {"entities" : qUnion([Q0, Q1, Q2, Q3, Q4, Q5, Q6]), "depth" : 17.14 * mm, "offsetDistance" : 25.4 * mm});
        }
        {
            var Q0;
            {var subQ18=sQuery(id+"F6.wireOp",EDGE,"E103");Q0=makeQuery(id+"F6.imprint","IMPRINT",FACE,{"disambiguationData":[TD([[makeQuery(id+"F6.imprint","IMPRINT",EDGE,{"derivedFrom":subQ18}),-1.0]])]});}
            var Q1;
            {var subQ0=sQuery(id+"F0.wireOp",EDGE,"E7.right");Q1=makeQuery(id+"F6.imprint","IMPRINT",FACE,{"disambiguationData":[TD([[makeQuery(id+"F6.imprint","IMPRINT",EDGE,{"derivedFrom":makeQuery(id+"F1.opExtrude","CAP_EDGE",EDGE,{"disambiguationData":[OSD([subQ0])],"isStart":false})}),-1.0]])]});}
            var Q2;
            {var subQ2=sQuery(id+"F0.wireOp",EDGE,"E35");Q2=makeQuery(id+"F6.imprint","IMPRINT",FACE,{"disambiguationData":[TD([[makeQuery(id+"F6.imprint","IMPRINT",EDGE,{"derivedFrom":makeQuery(id+"F1.opExtrude","CAP_EDGE",EDGE,{"disambiguationData":[OSD([subQ2])],"isStart":false})}),-1.0]])]});}
            var Q3;
            {var subQ0=sQuery(id+"F0.wireOp",EDGE,"E8.left");Q3=makeQuery(id+"F6.imprint","IMPRINT",FACE,{"disambiguationData":[TD([[makeQuery(id+"F6.imprint","IMPRINT",EDGE,{"derivedFrom":makeQuery(id+"F1.opExtrude","CAP_EDGE",EDGE,{"disambiguationData":[OSD([subQ0])],"isStart":false})}),-1.0]])]});}
            extrude(context, id + "F8", {"entities" : qUnion([Q0, Q1, Q2, Q3]), "depth" : 25.4 * mm, "offsetDistance" : 25.4 * mm});
        }
        {
            var Q0;
            {var subQ0=sQuery(id+"F6.wireOp",EDGE,"E106");Q0=makeQuery(id+"F6.imprint","IMPRINT",FACE,{"disambiguationData":[TD([[makeQuery(id+"F6.imprint","IMPRINT",EDGE,{"derivedFrom":subQ0}),-1.0]])]});}
            var Q1;
            {var subQ20=sQuery(id+"F6.wireOp",EDGE,"E108");Q1=makeQuery(id+"F6.imprint","IMPRINT",FACE,{"disambiguationData":[TD([[makeQuery(id+"F6.imprint","IMPRINT",EDGE,{"derivedFrom":subQ20}),-1.0]])]});}
            var Q2;
            {var subQ0=sQuery(id+"F0.wireOp",EDGE,"E9.right");Q2=makeQuery(id+"F6.imprint","IMPRINT",FACE,{"disambiguationData":[TD([[makeQuery(id+"F6.imprint","IMPRINT",EDGE,{"derivedFrom":makeQuery(id+"F1.opExtrude","CAP_EDGE",EDGE,{"disambiguationData":[OSD([subQ0])],"isStart":false})}),1.0]])]});}
            var Q3;
            {var subQ0=sQuery(id+"F0.wireOp",EDGE,"E39");Q3=makeQuery(id+"F6.imprint","IMPRINT",FACE,{"disambiguationData":[TD([[makeQuery(id+"F6.imprint","IMPRINT",EDGE,{"derivedFrom":makeQuery(id+"F1.opExtrude","CAP_EDGE",EDGE,{"disambiguationData":[OSD([subQ0])],"isStart":false})}),-1.0]])]});}
            var Q4;
            {var subQ0=sQuery(id+"F0.wireOp",EDGE,"E2.left");Q4=makeQuery(id+"F6.imprint","IMPRINT",FACE,{"disambiguationData":[TD([[makeQuery(id+"F6.imprint","IMPRINT",EDGE,{"derivedFrom":makeQuery(id+"F1.opExtrude","CAP_EDGE",EDGE,{"disambiguationData":[OSD([subQ0])],"isStart":false})}),-1.0]])]});}
            var Q5;
            {var subQ0=sQuery(id+"F6.wireOp",EDGE,"E111");Q5=makeQuery(id+"F6.imprint","IMPRINT",FACE,{"disambiguationData":[TD([[makeQuery(id+"F6.imprint","IMPRINT",EDGE,{"derivedFrom":subQ0}),-1.0]])]});}
            var Q6;
            {var subQ0=sQuery(id+"F6.wireOp",EDGE,"E110");var subQ3=makeQuery(id+"F1.opExtrude","CAP_EDGE",EDGE,{"disambiguationData":[OSD([sQuery(id+"F0.wireOp",EDGE,"E3.right")])],"isStart":false});var subQ4=makeQuery(id+"F6.imprint","INTERSECT",VERTEX,{"derivedFrom":[subQ3,subQ0]});Q6=makeQuery(id+"F6.imprint","IMPRINT",FACE,{"disambiguationData":[TD([[makeQuery(id+"F6.imprint","IMPRINT",EDGE,{"disambiguationData":[TD([[subQ4,-1.0]])],"derivedFrom":subQ3}),-1.0]])]});}
            extrude(context, id + "F9", {"entities" : qUnion([Q0, Q1, Q2, Q3, Q4, Q5, Q6]), "depth" : 25.4 * mm, "offsetDistance" : 25.4 * mm});
        }
    });
